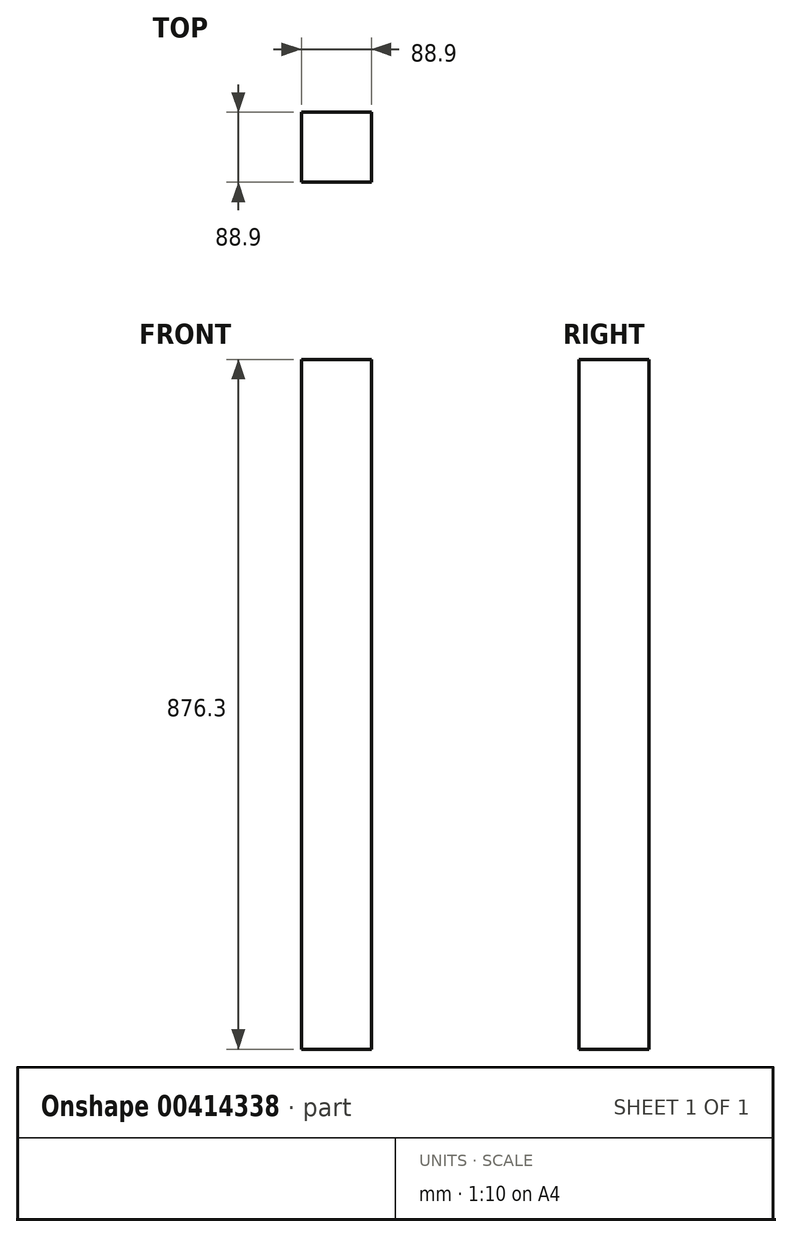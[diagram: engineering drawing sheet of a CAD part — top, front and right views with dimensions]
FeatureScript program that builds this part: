
annotation { "Feature Type Name" : "Feature", "Feature Type Description" : "" }
export const myFeature = defineFeature(function(context is Context, id is Id, definition is map)
    precondition{}
    {
        {
            var Q0;
            Q0=qCreatedBy(makeId("Top.planeOp"),FACE);
            var sketch = newSketch(context, id + "F0", { "sketchPlane" : qUnion([Q0])});
            skLineSegment(sketch, "E0.bottom", {"start": v(44.45, 44.45) * mm, "end": v(-44.45, 44.45) * mm});
            skLineSegment(sketch, "E0.top", {"start": v(44.45, -44.45) * mm, "end": v(-44.45, -44.45) * mm});
            skLineSegment(sketch, "E0.left", {"start": v(44.45, 44.45) * mm, "end": v(44.45, -44.45) * mm});
            skLineSegment(sketch, "E0.right", {"start": v(-44.45, 44.45) * mm, "end": v(-44.45, -44.45) * mm});
            skPoint(sketch, "E0.middle", {"position": v(0, 0) * mm});
            skSolve(sketch);
        }
        {
            var Q0;
            Q0 = qSketchRegion(id + "F0", true);
            extrude(context, id + "F1", {"entities" : qUnion([Q0]), "depth" : 876.3 * mm});
        }
    });
